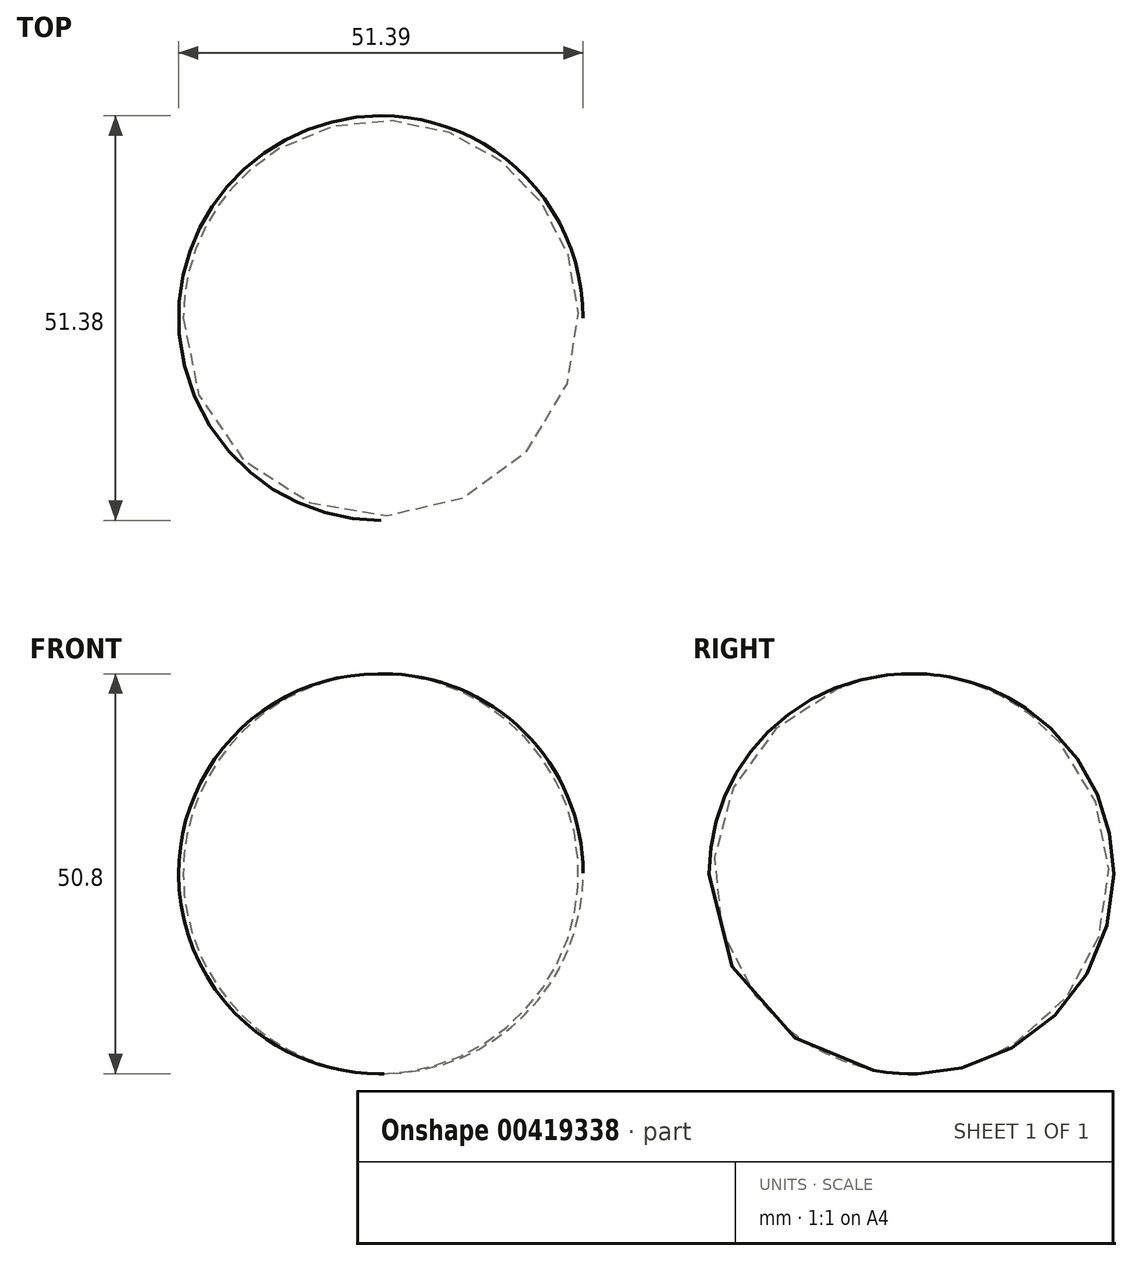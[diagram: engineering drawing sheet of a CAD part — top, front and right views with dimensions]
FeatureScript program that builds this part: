
annotation { "Feature Type Name" : "Feature", "Feature Type Description" : "" }
export const myFeature = defineFeature(function(context is Context, id is Id, definition is map)
    precondition{}
    {
        {
            var Q0;
            Q0=qCreatedBy(makeId("Front.planeOp"),FACE);
            var sketch = newSketch(context, id + "F0", { "sketchPlane" : qUnion([Q0])});
            skArc(sketch, "E0", {"start": v(0.2, 25.4) * mm, "mid": v(-25.4, -0.09) * mm, "end": v(0.38, -25.4) * mm});
            skLineSegment(sketch, "E1", {"start": v(0.2, 25.4) * mm, "end": v(0.38, -25.4) * mm});
            skSolve(sketch);
        }
        {
            var Q0;
            Q0 = qSketchRegion(id + "F0", true);
            var Q1;
            Q1=sQuery(id+"F0.wireOp",EDGE,"E1");
            revolve(context, id + "F1", {"entities" : qUnion([Q0]), "axis" : qUnion([Q1]), "revolveType" : RevolveType.FULL});
        }
    });
